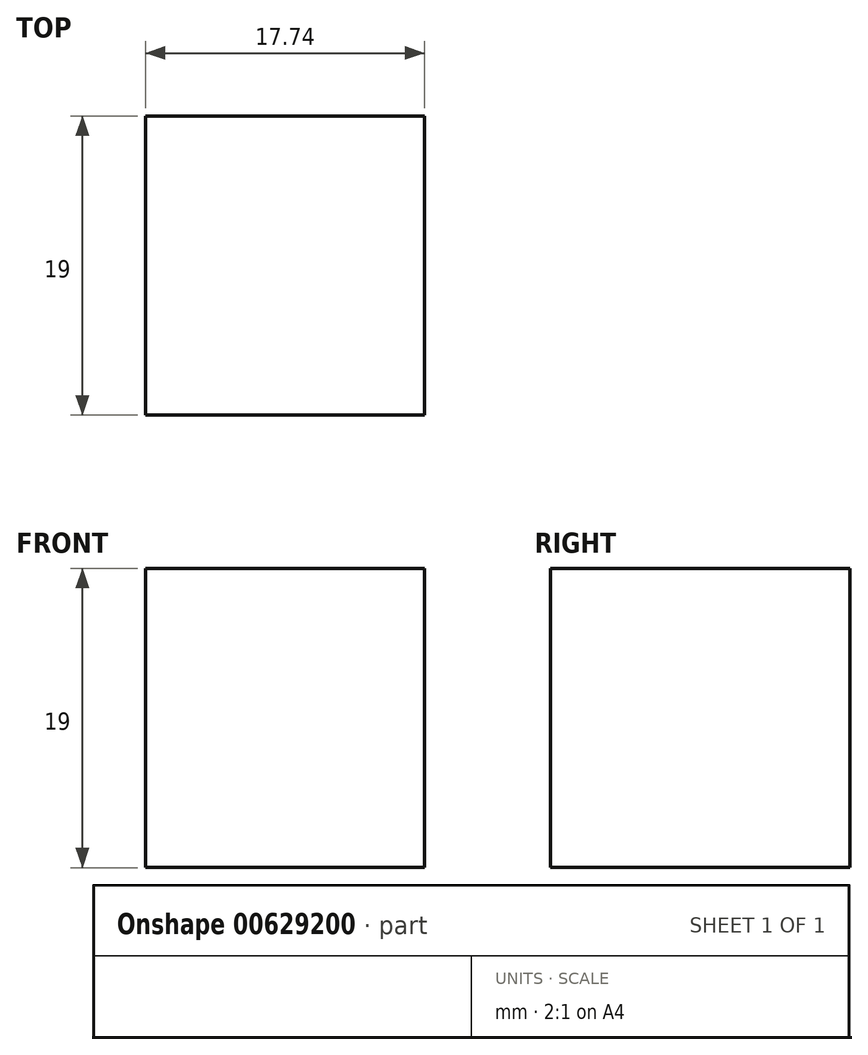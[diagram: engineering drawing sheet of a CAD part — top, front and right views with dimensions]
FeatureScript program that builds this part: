
annotation { "Feature Type Name" : "Feature", "Feature Type Description" : "" }
export const myFeature = defineFeature(function(context is Context, id is Id, definition is map)
    precondition{}
    {
        {
            var Q0;
            Q0=qCreatedBy(makeId("Front.planeOp"),FACE);
            var sketch = newSketch(context, id + "F0", { "sketchPlane" : qUnion([Q0])});
            skLineSegment(sketch, "E0.bottom", {"start": v(8.87, 9.5) * mm, "end": v(-8.87, 9.5) * mm});
            skLineSegment(sketch, "E0.top", {"start": v(8.87, -9.5) * mm, "end": v(-8.87, -9.5) * mm});
            skLineSegment(sketch, "E0.left", {"start": v(8.87, 9.5) * mm, "end": v(8.87, -9.5) * mm});
            skLineSegment(sketch, "E0.right", {"start": v(-8.87, 9.5) * mm, "end": v(-8.87, -9.5) * mm});
            skPoint(sketch, "E0.middle", {"position": v(0, 0) * mm});
            skSolve(sketch);
        }
        {
            var Q0;
            Q0 = qSketchRegion(id + "F0", true);
            var Q1;
            Q1=makeQuery(id+"F0.imprint","IMPRINT",FACE,{"disambiguationData":[TD([[makeQuery(id+"F0.imprint","IMPRINT",EDGE,{"derivedFrom":sQuery(id+"F0.wireOp",EDGE,"E0.bottom")}),1.0]])]});
            extrude(context, id + "F1", {"entities" : qUnion([Q0, Q1]), "depth" : 19 * mm, "offsetDistance" : 25 * mm});
        }
    });
